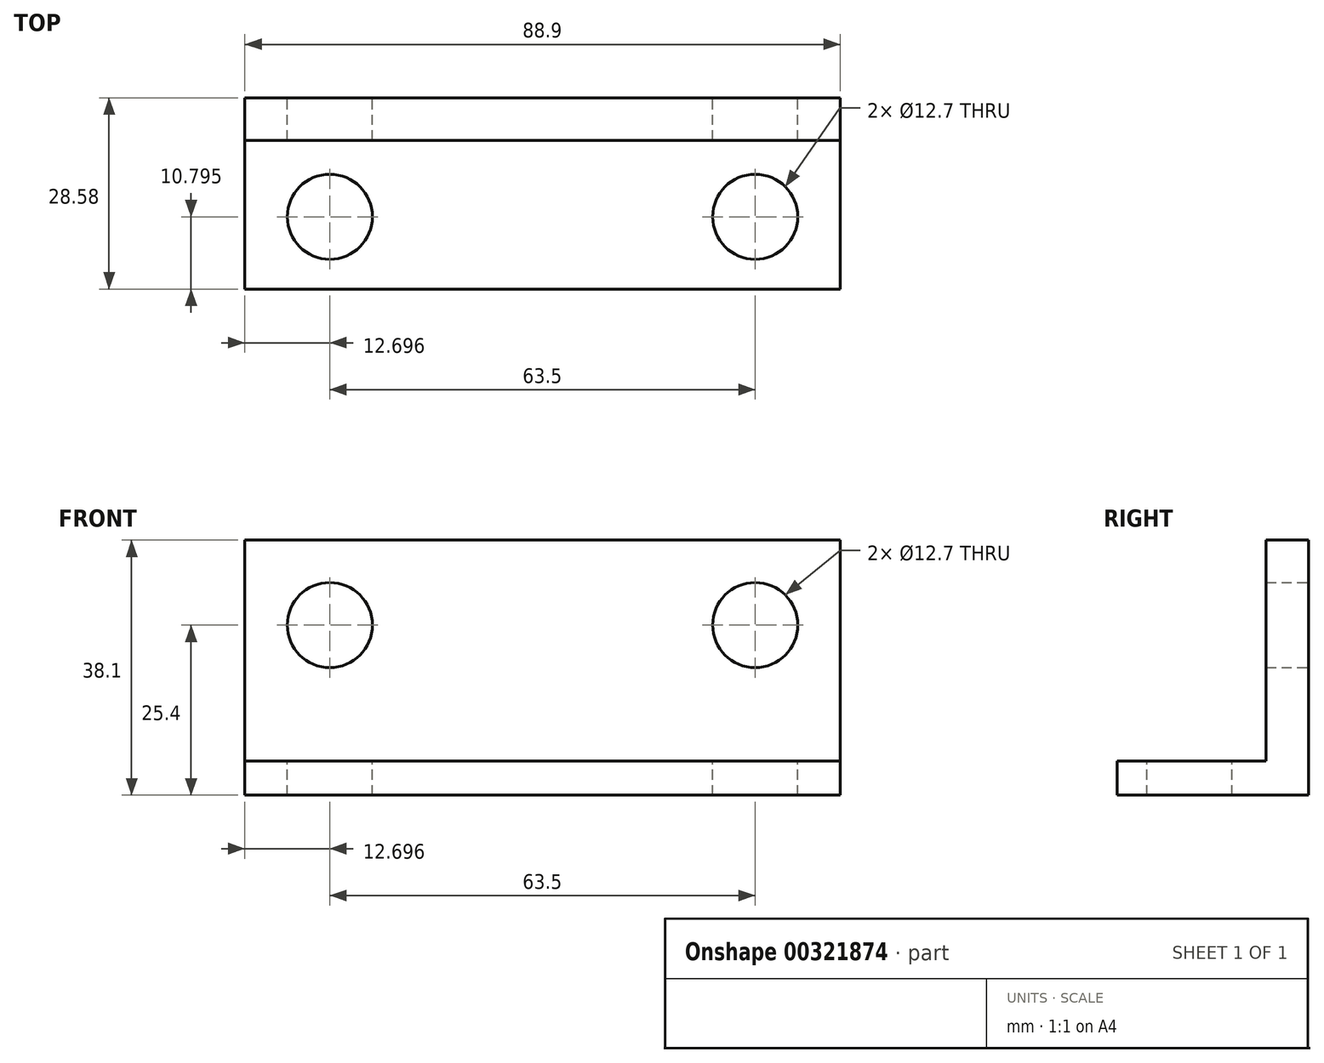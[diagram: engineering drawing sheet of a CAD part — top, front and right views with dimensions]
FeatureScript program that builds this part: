
annotation { "Feature Type Name" : "Feature", "Feature Type Description" : "" }
export const myFeature = defineFeature(function(context is Context, id is Id, definition is map)
    precondition{}
    {
        {
            var Q0;
            Q0=qCreatedBy(makeId("Front.planeOp"),FACE);
            var sketch = newSketch(context, id + "F0", { "sketchPlane" : qUnion([Q0])});
            skLineSegment(sketch, "E0.bottom", {"start": v(-71.06, 12.7) * mm, "end": v(17.84, 12.7) * mm});
            skLineSegment(sketch, "E0.top", {"start": v(-71.06, -25.4) * mm, "end": v(17.84, -25.4) * mm});
            skLineSegment(sketch, "E0.left", {"start": v(-71.06, 12.7) * mm, "end": v(-71.06, -25.4) * mm});
            skLineSegment(sketch, "E0.right", {"start": v(17.84, 12.7) * mm, "end": v(17.84, -25.4) * mm});
            skLineSegment(sketch, "E1.top", {"start": v(-71.06, -20.32) * mm, "end": v(17.84, -20.32) * mm});
            skLineSegment(sketch, "E1.left", {"start": v(-71.06, -25.4) * mm, "end": v(-71.06, -20.32) * mm});
            skLineSegment(sketch, "E1.right", {"start": v(17.84, -25.4) * mm, "end": v(17.84, -20.32) * mm});
            skCircle(sketch, "E2", {"center": v(-58.36, 0) * mm, "radius": 6.35 * mm});
            skCircle(sketch, "E3", {"center": v(5.14, 0) * mm, "radius": 6.35 * mm});
            skSolve(sketch);
        }
        {
            var Q0;
            Q0=makeQuery(id+"F0.imprint","IMPRINT",FACE,{"disambiguationData":[TD([[makeQuery(id+"F0.imprint","IMPRINT",EDGE,{"derivedFrom":sQuery(id+"F0.wireOp",EDGE,"E0.bottom")}),-1.0]])]});
            extrude(context, id + "F1", {"entities" : qUnion([Q0]), "endBound" : BoundingType.SYMMETRIC, "depth" : 6.35 * mm});
        }
        {
            var Q0;
            Q0=makeQuery(id+"F0.imprint","IMPRINT",FACE,{"disambiguationData":[TD([[makeQuery(id+"F0.imprint","IMPRINT",EDGE,{"derivedFrom":sQuery(id+"F0.wireOp",EDGE,"E0.top")}),1.0]])]});
            extrude(context, id + "F2", {"entities" : qUnion([Q0]), "operationType" : NewBodyOperationType.ADD, "depth" : 25.4 * mm});
        }
        {
            var Q0;
            Q0=makeQuery(id+"F0.imprint","IMPRINT",FACE,{"disambiguationData":[TD([[makeQuery(id+"F0.imprint","IMPRINT",EDGE,{"derivedFrom":sQuery(id+"F0.wireOp",EDGE,"E0.top")}),1.0]])]});
            extrude(context, id + "F3", {"entities" : qUnion([Q0]), "operationType" : NewBodyOperationType.ADD, "oppositeDirection" : true, "depth" : 3.17 * mm});
        }
        {
            var Q0;
            Q0=qCreatedBy(makeId("Top.planeOp"),FACE);
            var sketch = newSketch(context, id + "F4", { "sketchPlane" : qUnion([Q0])});
            skPoint(sketch, "E4", {"position": v(-58.36, -14.6) * mm});
            skPoint(sketch, "E5", {"position": v(5.14, -14.6) * mm});
            skSolve(sketch);
        }
        {
            var Q0;
            Q0=sQuery(id+"F4.wireOp",VERTEX,"E4");
            var Q1;
            Q1=sQuery(id+"F4.wireOp",VERTEX,"E5");
            var Q2;
            Q2=makeQuery(id+"F1.opExtrude","SWEPT_BODY",BODY,{"disambiguationData":[OSD([sQuery(id+"F0.wireOp",EDGE,"E0.bottom"),sQuery(id+"F0.wireOp",EDGE,"E0.left"),sQuery(id+"F0.wireOp",EDGE,"E0.right"),sQuery(id+"F0.wireOp",EDGE,"E1.top"),sQuery(id+"F0.wireOp",EDGE,"E2"),sQuery(id+"F0.wireOp",EDGE,"E3")])]});
            hole(context, id + "F5", {"style" : HoleStyle.SIMPLE, "endStyle" : HoleEndStyle.THROUGH, "holeDiameter" : 12.7 * mm, "tappedDepth" : 12.7 * mm, "tapClearance" : 3, "locations" : qUnion([Q0, Q1]), "scope" : qUnion([Q2])});
        }
    });
